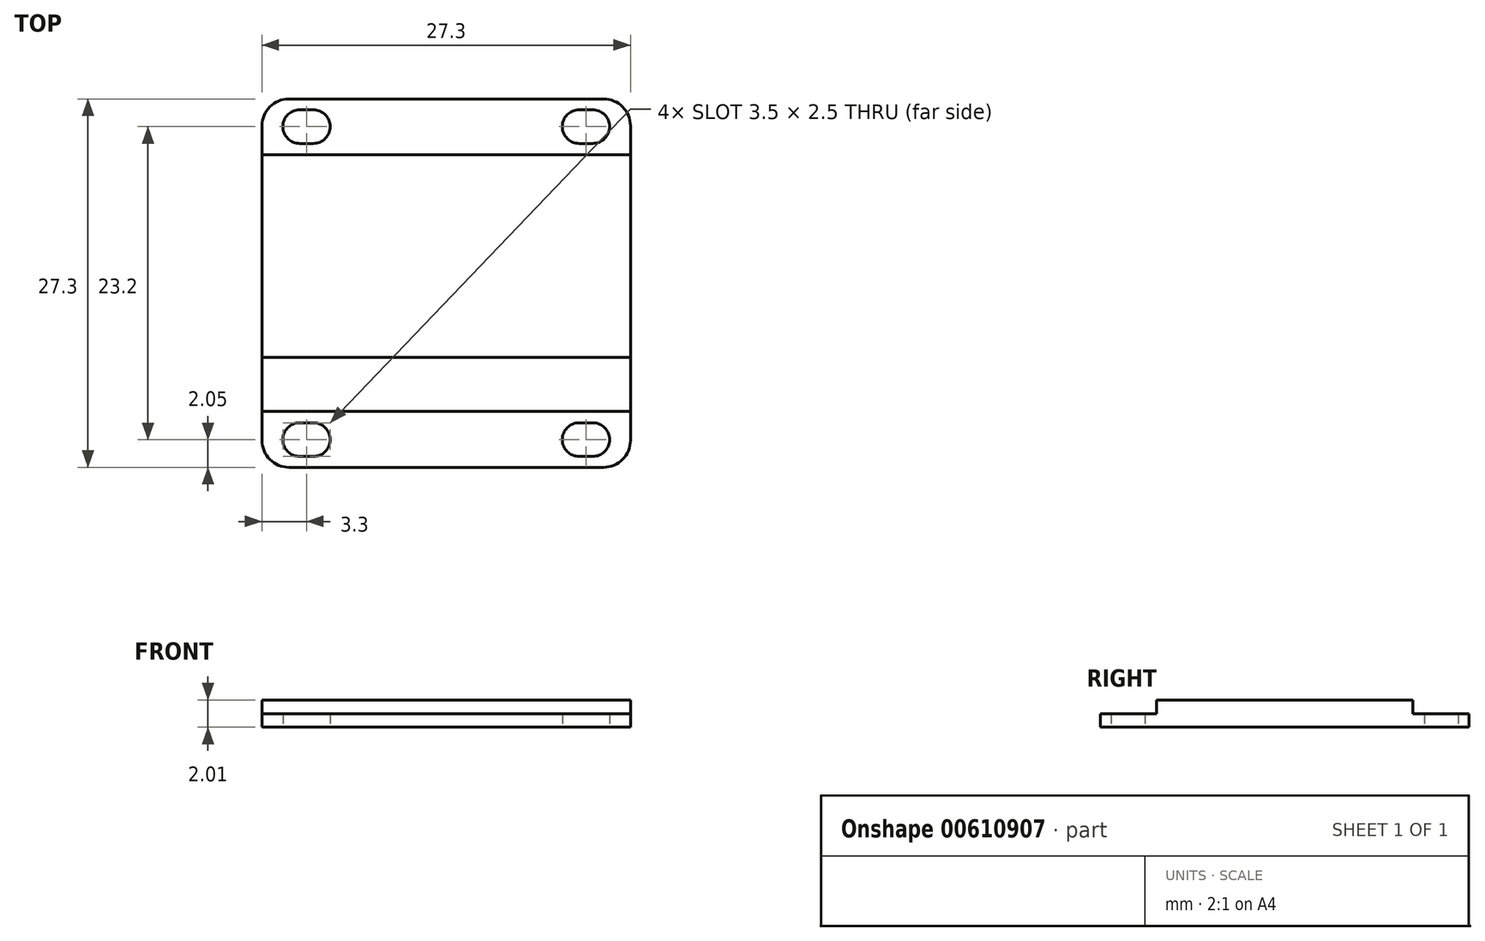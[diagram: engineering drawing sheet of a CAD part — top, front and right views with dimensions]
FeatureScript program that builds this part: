
annotation { "Feature Type Name" : "Feature", "Feature Type Description" : "" }
export const myFeature = defineFeature(function(context is Context, id is Id, definition is map)
    precondition{}
    {
        {
            var Q0;
            Q0=qCreatedBy(makeId("Top.planeOp"),FACE);
            var sketch = newSketch(context, id + "F0", { "sketchPlane" : qUnion([Q0])});
            skLineSegment(sketch, "E0.bottom", {"start": v(11.65, -13.65) * mm, "end": v(-11.65, -13.65) * mm});
            skLineSegment(sketch, "E0.top", {"start": v(11.65, 13.65) * mm, "end": v(-11.65, 13.65) * mm});
            skLineSegment(sketch, "E0.left", {"start": v(13.65, -11.65) * mm, "end": v(13.65, 11.65) * mm});
            skLineSegment(sketch, "E0.right", {"start": v(-13.65, -11.65) * mm, "end": v(-13.65, 11.65) * mm});
            skPoint(sketch, "E0.middle", {"position": v(0, 0) * mm});
            skLineSegment(sketch, "E1.bottom", {"start": v(-9.85, 10.35) * mm, "end": v(-10.85, 10.35) * mm});
            skLineSegment(sketch, "E1.top", {"start": v(-9.85, 12.85) * mm, "end": v(-10.85, 12.85) * mm});
            skLineSegment(sketch, "E1.left", {"start": v(-8.6, 11.6) * mm, "end": v(-8.6, 11.6) * mm});
            skLineSegment(sketch, "E1.right", {"start": v(-12.1, 11.6) * mm, "end": v(-12.1, 11.6) * mm});
            skPoint(sketch, "E1.middle", {"position": v(-10.35, 11.6) * mm});
            skPoint(sketch, "E2.visualSharp", {"position": v(-8.6, 12.85) * mm});
            skArc(sketch, "E2.filletArc", {"start": v(-8.6, 11.6) * mm, "mid": v(-8.97, 12.48) * mm, "end": v(-9.85, 12.85) * mm});
            skPoint(sketch, "E3.visualSharp", {"position": v(-8.6, 10.35) * mm});
            skArc(sketch, "E3.filletArc", {"start": v(-9.85, 10.35) * mm, "mid": v(-8.97, 10.72) * mm, "end": v(-8.6, 11.6) * mm});
            skPoint(sketch, "E4.visualSharp", {"position": v(-12.1, 10.35) * mm});
            skArc(sketch, "E4.filletArc", {"start": v(-12.1, 11.6) * mm, "mid": v(-11.73, 10.72) * mm, "end": v(-10.85, 10.35) * mm});
            skPoint(sketch, "E5.visualSharp", {"position": v(-12.1, 12.85) * mm});
            skArc(sketch, "E5.filletArc", {"start": v(-10.85, 12.85) * mm, "mid": v(-11.73, 12.48) * mm, "end": v(-12.1, 11.6) * mm});
            skPoint(sketch, "E6.MirrorP", {"position": v(-8.6, -10.35) * mm});
            skLineSegment(sketch, "E7.MirrorCS", {"start": v(-8.6, -11.6) * mm, "end": v(-8.6, -11.6) * mm});
            skPoint(sketch, "E8.MirrorP", {"position": v(-10.35, -11.6) * mm});
            skPoint(sketch, "E9.MirrorP", {"position": v(-12.1, -10.35) * mm});
            skPoint(sketch, "E10.MirrorP", {"position": v(-12.1, -12.85) * mm});
            skArc(sketch, "E11.MirrorCS", {"start": v(-10.85, -12.85) * mm, "mid": v(-11.73, -12.48) * mm, "end": v(-12.1, -11.6) * mm});
            skArc(sketch, "E12.MirrorCS", {"start": v(-8.6, -11.6) * mm, "mid": v(-8.97, -12.48) * mm, "end": v(-9.85, -12.85) * mm});
            skPoint(sketch, "E13.MirrorP", {"position": v(-8.6, -12.85) * mm});
            skArc(sketch, "E14.MirrorCS", {"start": v(-9.85, -10.35) * mm, "mid": v(-8.97, -10.72) * mm, "end": v(-8.6, -11.6) * mm});
            skLineSegment(sketch, "E15.MirrorCS", {"start": v(-9.85, -12.85) * mm, "end": v(-10.85, -12.85) * mm});
            skLineSegment(sketch, "E16.MirrorCS", {"start": v(-9.85, -10.35) * mm, "end": v(-10.85, -10.35) * mm});
            skArc(sketch, "E17.MirrorCS", {"start": v(-12.1, -11.6) * mm, "mid": v(-11.73, -10.72) * mm, "end": v(-10.85, -10.35) * mm});
            skLineSegment(sketch, "E18.MirrorCS", {"start": v(-12.1, -11.6) * mm, "end": v(-12.1, -11.6) * mm});
            skPoint(sketch, "E19.MirrorP", {"position": v(10.35, -11.6) * mm});
            skArc(sketch, "E20.MirrorCS", {"start": v(9.85, -10.35) * mm, "mid": v(8.97, -10.72) * mm, "end": v(8.6, -11.6) * mm});
            skArc(sketch, "E21.MirrorCS", {"start": v(8.6, -11.6) * mm, "mid": v(8.97, -12.48) * mm, "end": v(9.85, -12.85) * mm});
            skArc(sketch, "E22.MirrorCS", {"start": v(10.85, -12.85) * mm, "mid": v(11.73, -12.48) * mm, "end": v(12.1, -11.6) * mm});
            skPoint(sketch, "E23.MirrorP", {"position": v(8.6, -12.85) * mm});
            skLineSegment(sketch, "E24.MirrorCS", {"start": v(8.6, -11.6) * mm, "end": v(8.6, -11.6) * mm});
            skLineSegment(sketch, "E25.MirrorCS", {"start": v(12.1, -11.6) * mm, "end": v(12.1, -11.6) * mm});
            skPoint(sketch, "E26.MirrorP", {"position": v(12.1, -12.85) * mm});
            skPoint(sketch, "E27.MirrorP", {"position": v(8.6, -10.35) * mm});
            skLineSegment(sketch, "E28.MirrorCS", {"start": v(9.85, -12.85) * mm, "end": v(10.85, -12.85) * mm});
            skPoint(sketch, "E29.MirrorP", {"position": v(12.1, -10.35) * mm});
            skLineSegment(sketch, "E30.MirrorCS", {"start": v(9.85, -10.35) * mm, "end": v(10.85, -10.35) * mm});
            skArc(sketch, "E31.MirrorCS", {"start": v(12.1, -11.6) * mm, "mid": v(11.73, -10.72) * mm, "end": v(10.85, -10.35) * mm});
            skLineSegment(sketch, "E32.MirrorCS", {"start": v(9.85, 12.85) * mm, "end": v(10.85, 12.85) * mm});
            skPoint(sketch, "E33.MirrorP", {"position": v(10.35, 11.6) * mm});
            skLineSegment(sketch, "E34.MirrorCS", {"start": v(12.1, 11.6) * mm, "end": v(12.1, 11.6) * mm});
            skPoint(sketch, "E35.MirrorP", {"position": v(12.1, 10.35) * mm});
            skLineSegment(sketch, "E36.MirrorCS", {"start": v(8.6, 11.6) * mm, "end": v(8.6, 11.6) * mm});
            skLineSegment(sketch, "E37.MirrorCS", {"start": v(9.85, 10.35) * mm, "end": v(10.85, 10.35) * mm});
            skPoint(sketch, "E38.MirrorP", {"position": v(8.6, 10.35) * mm});
            skArc(sketch, "E39.MirrorCS", {"start": v(8.6, 11.6) * mm, "mid": v(8.97, 12.48) * mm, "end": v(9.85, 12.85) * mm});
            skArc(sketch, "E40.MirrorCS", {"start": v(9.85, 10.35) * mm, "mid": v(8.97, 10.72) * mm, "end": v(8.6, 11.6) * mm});
            skArc(sketch, "E41.MirrorCS", {"start": v(12.1, 11.6) * mm, "mid": v(11.73, 10.72) * mm, "end": v(10.85, 10.35) * mm});
            skArc(sketch, "E42.MirrorCS", {"start": v(10.85, 12.85) * mm, "mid": v(11.73, 12.48) * mm, "end": v(12.1, 11.6) * mm});
            skPoint(sketch, "E43.MirrorP", {"position": v(12.1, 12.85) * mm});
            skPoint(sketch, "E44.MirrorP", {"position": v(8.6, 12.85) * mm});
            skPoint(sketch, "E45.visualSharp", {"position": v(13.65, 13.65) * mm});
            skArc(sketch, "E45.filletArc", {"start": v(13.65, 11.65) * mm, "mid": v(13.06, 13.06) * mm, "end": v(11.65, 13.65) * mm});
            skPoint(sketch, "E46.visualSharp", {"position": v(13.65, -13.65) * mm});
            skArc(sketch, "E46.filletArc", {"start": v(11.65, -13.65) * mm, "mid": v(13.06, -13.06) * mm, "end": v(13.65, -11.65) * mm});
            skPoint(sketch, "E47.visualSharp", {"position": v(-13.65, -13.65) * mm});
            skArc(sketch, "E47.filletArc", {"start": v(-13.65, -11.65) * mm, "mid": v(-13.06, -13.06) * mm, "end": v(-11.65, -13.65) * mm});
            skPoint(sketch, "E48.visualSharp", {"position": v(-13.65, 13.65) * mm});
            skArc(sketch, "E48.filletArc", {"start": v(-11.65, 13.65) * mm, "mid": v(-13.06, 13.06) * mm, "end": v(-13.65, 11.65) * mm});
            skSolve(sketch);
        }
        {
            var Q0;
            Q0 = qSketchRegion(id + "F0", true);
            extrude(context, id + "F1", {"entities" : qUnion([Q0]), "depth" : 1 * mm, "offsetDistance" : 25 * mm});
        }
        {
            var Q0;
            Q0=makeQuery(id+"F1.opExtrude","CAP_FACE",FACE,{"disambiguationData":[OSD([sQuery(id+"F0.wireOp",EDGE,"E0.bottom"),sQuery(id+"F0.wireOp",EDGE,"E0.top"),sQuery(id+"F0.wireOp",EDGE,"E0.left"),sQuery(id+"F0.wireOp",EDGE,"E0.right"),sQuery(id+"F0.wireOp",EDGE,"E1.bottom"),sQuery(id+"F0.wireOp",EDGE,"E1.top"),sQuery(id+"F0.wireOp",EDGE,"E2.filletArc"),sQuery(id+"F0.wireOp",EDGE,"E3.filletArc"),sQuery(id+"F0.wireOp",EDGE,"E4.filletArc"),sQuery(id+"F0.wireOp",EDGE,"E5.filletArc"),sQuery(id+"F0.wireOp",EDGE,"E11.MirrorCS"),sQuery(id+"F0.wireOp",EDGE,"E12.MirrorCS"),sQuery(id+"F0.wireOp",EDGE,"E14.MirrorCS"),sQuery(id+"F0.wireOp",EDGE,"E15.MirrorCS"),sQuery(id+"F0.wireOp",EDGE,"E16.MirrorCS"),sQuery(id+"F0.wireOp",EDGE,"E17.MirrorCS"),sQuery(id+"F0.wireOp",EDGE,"E20.MirrorCS"),sQuery(id+"F0.wireOp",EDGE,"E21.MirrorCS"),sQuery(id+"F0.wireOp",EDGE,"E22.MirrorCS"),sQuery(id+"F0.wireOp",EDGE,"E28.MirrorCS"),sQuery(id+"F0.wireOp",EDGE,"E30.MirrorCS"),sQuery(id+"F0.wireOp",EDGE,"E31.MirrorCS"),sQuery(id+"F0.wireOp",EDGE,"E32.MirrorCS"),sQuery(id+"F0.wireOp",EDGE,"E37.MirrorCS"),sQuery(id+"F0.wireOp",EDGE,"E39.MirrorCS"),sQuery(id+"F0.wireOp",EDGE,"E40.MirrorCS"),sQuery(id+"F0.wireOp",EDGE,"E41.MirrorCS"),sQuery(id+"F0.wireOp",EDGE,"E42.MirrorCS"),sQuery(id+"F0.wireOp",EDGE,"E45.filletArc"),sQuery(id+"F0.wireOp",EDGE,"E46.filletArc"),sQuery(id+"F0.wireOp",EDGE,"E47.filletArc"),sQuery(id+"F0.wireOp",EDGE,"E48.filletArc")])],"isStart":false});
            var sketch = newSketch(context, id + "F2", { "sketchPlane" : qUnion([Q0])});
            skLineSegment(sketch, "E49.bottom", {"start": v(13.65, -9.5) * mm, "end": v(-13.65, -9.5) * mm});
            skLineSegment(sketch, "E49.top", {"start": v(13.65, 9.5) * mm, "end": v(-13.65, 9.5) * mm});
            skLineSegment(sketch, "E49.left", {"start": v(13.65, -9.5) * mm, "end": v(13.65, 9.5) * mm});
            skLineSegment(sketch, "E49.right", {"start": v(-13.65, -9.5) * mm, "end": v(-13.65, 9.5) * mm});
            skPoint(sketch, "E49.middle", {"position": v(0, 0) * mm});
            skSolve(sketch);
        }
        {
            var Q0;
            Q0 = qSketchRegion(id + "F2", true);
            extrude(context, id + "F3", {"entities" : qUnion([Q0]), "operationType" : NewBodyOperationType.ADD, "depth" : 1 * mm, "offsetDistance" : 25 * mm});
        }
        {
            var Q0;
            Q0=makeQuery(id+"F3.opExtrude","CAP_FACE",FACE,{"disambiguationData":[OSD([sQuery(id+"F2.wireOp",EDGE,"E49.bottom"),sQuery(id+"F2.wireOp",EDGE,"E49.top"),sQuery(id+"F2.wireOp",EDGE,"E49.left"),sQuery(id+"F2.wireOp",EDGE,"E49.right")])],"isStart":false});
            var sketch = newSketch(context, id + "F4", { "sketchPlane" : qUnion([Q0])});
            skLineSegment(sketch, "E50.bottom", {"start": v(-13.65, 9.5) * mm, "end": v(13.65, 9.5) * mm});
            skLineSegment(sketch, "E50.top", {"start": v(-13.65, -5.5) * mm, "end": v(13.65, -5.5) * mm});
            skLineSegment(sketch, "E50.left", {"start": v(-13.65, 9.5) * mm, "end": v(-13.65, -5.5) * mm});
            skLineSegment(sketch, "E50.right", {"start": v(13.65, 9.5) * mm, "end": v(13.65, -5.5) * mm});
            skSolve(sketch);
        }
        {
            var Q0;
            Q0 = qSketchRegion(id + "F4", true);
            extrude(context, id + "F5", {"entities" : qUnion([Q0]), "operationType" : NewBodyOperationType.ADD, "depth" : 0.01 * mm, "offsetDistance" : 25 * mm});
        }
    });
